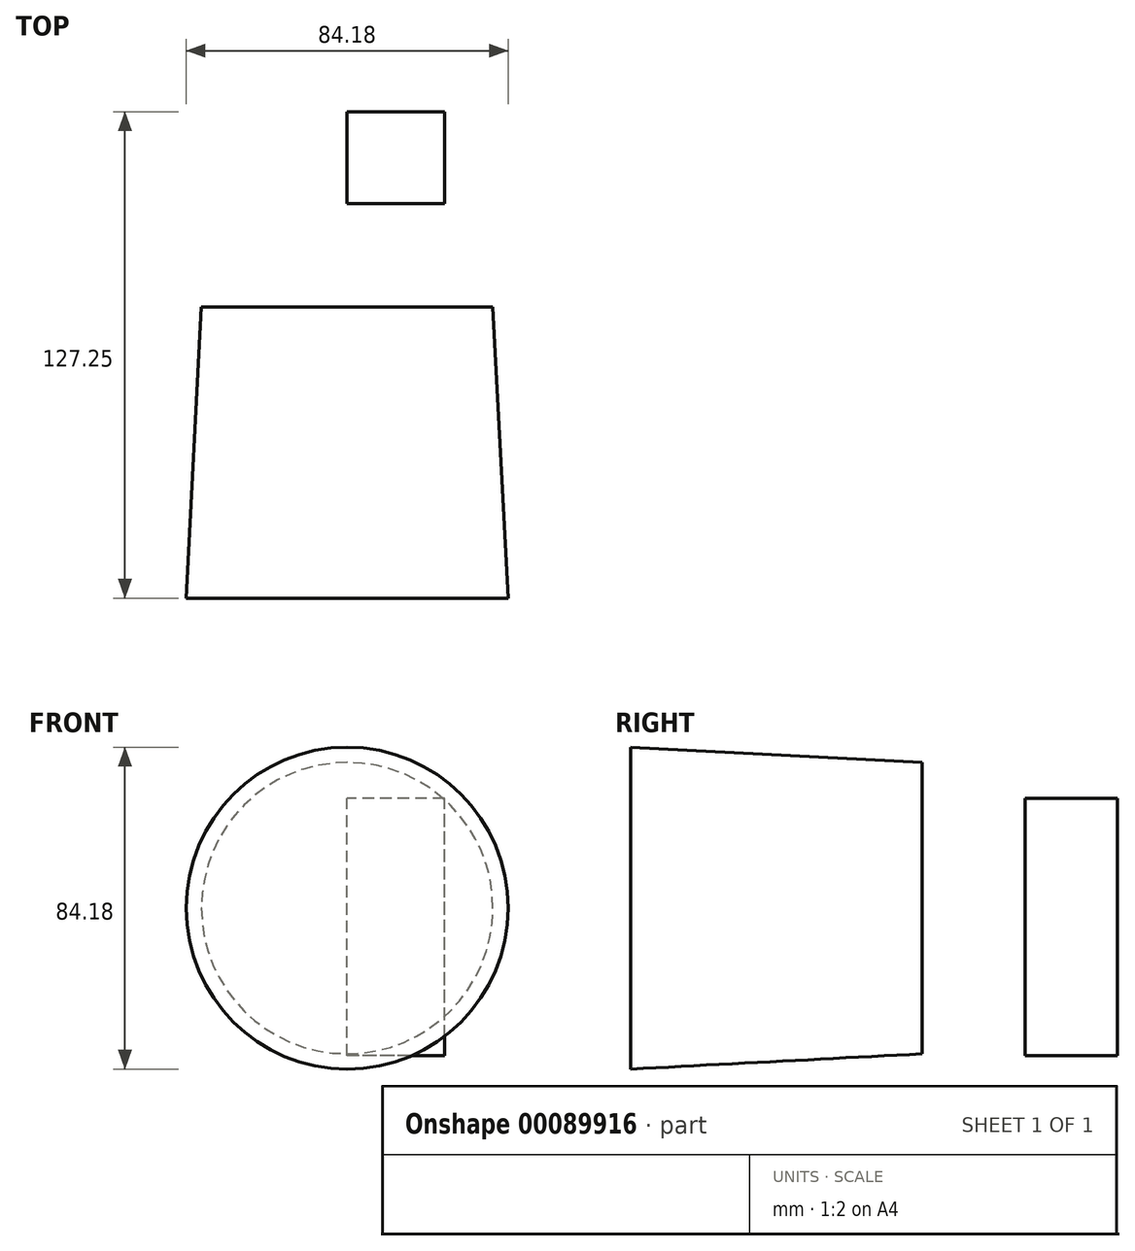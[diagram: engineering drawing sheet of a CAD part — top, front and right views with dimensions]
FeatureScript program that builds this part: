
annotation { "Feature Type Name" : "Feature", "Feature Type Description" : "" }
export const myFeature = defineFeature(function(context is Context, id is Id, definition is map)
    precondition{}
    {
        {
            var Q0;
            Q0=qCreatedBy(makeId("Front.planeOp"),FACE);
            var sketch = newSketch(context, id + "F0", { "sketchPlane" : qUnion([Q0])});
            skCircle(sketch, "E0", {"center": v(0, 0) * mm, "radius": 38.1 * mm});
            skSolve(sketch);
        }
        {
            var Q0;
            Q0=makeQuery(id+"F0.imprint","IMPRINT",FACE,{"disambiguationData":[TD([[makeQuery(id+"F0.imprint","IMPRINT",EDGE,{"derivedFrom":sQuery(id+"F0.wireOp",EDGE,"E0")}),1.0]])]});
            extrude(context, id + "F1", {"entities" : qUnion([Q0]), "depth" : 76.2 * mm, "hasDraft" : true, "draftAngle" : 3 * degree});
        }
        {
            var Q0;
            Q0=qCreatedBy(makeId("Right.planeOp"),FACE);
            var sketch = newSketch(context, id + "F2", { "sketchPlane" : qUnion([Q0])});
            skLineSegment(sketch, "E1.bottom", {"start": v(27, -38.53) * mm, "end": v(51.05, -38.53) * mm});
            skLineSegment(sketch, "E1.top", {"start": v(27, 28.72) * mm, "end": v(51.05, 28.72) * mm});
            skLineSegment(sketch, "E1.left", {"start": v(27, -38.53) * mm, "end": v(27, 28.72) * mm});
            skLineSegment(sketch, "E1.right", {"start": v(51.05, -38.53) * mm, "end": v(51.05, 28.72) * mm});
            skSolve(sketch);
        }
        {
            var Q0;
            Q0 = qSketchRegion(id + "F2", true);
            extrude(context, id + "F3", {"entities" : qUnion([Q0]), "depth" : 25.4 * mm});
        }
    });
